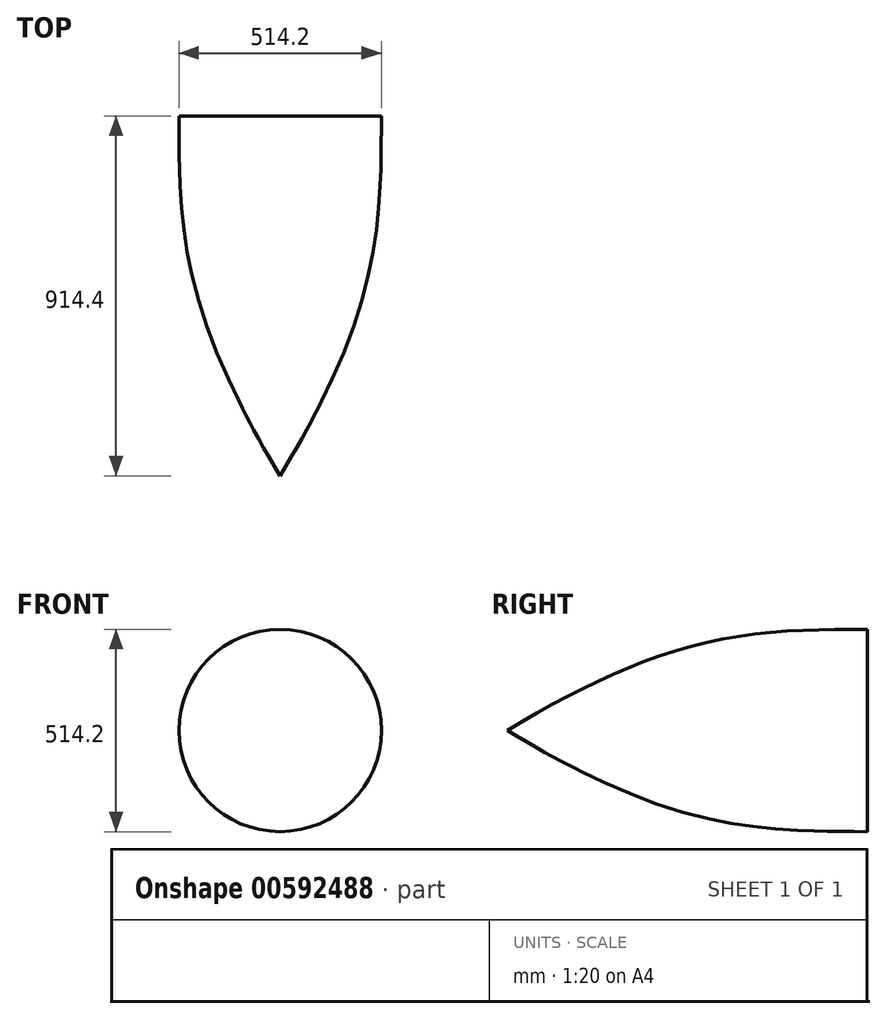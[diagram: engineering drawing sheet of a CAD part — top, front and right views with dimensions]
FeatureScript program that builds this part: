
annotation { "Feature Type Name" : "Feature", "Feature Type Description" : "" }
export const myFeature = defineFeature(function(context is Context, id is Id, definition is map)
    precondition{}
    {
        {
            var Q0;
            Q0=qCreatedBy(makeId("Right.planeOp"),FACE);
            var sketch = newSketch(context, id + "F0", { "sketchPlane" : qUnion([Q0])});
            skLineSegment(sketch, "E0", {"start": v(-457.2, 0) * mm, "end": v(457.2, 0) * mm});
            skLineSegment(sketch, "E1", {"start": v(457.2, 0) * mm, "end": v(457.2, 257.1) * mm});
            skPoint(sketch, "E2", {"position": v(-355.6, 58.93) * mm});
            skPoint(sketch, "E3", {"position": v(-254, 111.5) * mm});
            skPoint(sketch, "E4", {"position": v(-152.4, 157.78) * mm});
            skPoint(sketch, "E5", {"position": v(50.8, 223.82) * mm});
            skPoint(sketch, "E6", {"position": v(152.4, 242.32) * mm});
            skPoint(sketch, "E7", {"position": v(254, 252.63) * mm});
            skPoint(sketch, "E8", {"position": v(-50.8, 195.6) * mm});
            skPoint(sketch, "E9", {"position": v(355.6, 256.29) * mm});
            skFitSpline(sketch, "E10", {"points": [v(-457.2, 0) * mm, v(-355.6, 58.93) * mm, v(-254, 111.5) * mm, v(-152.4, 157.78) * mm, v(-50.8, 195.6) * mm, v(50.8, 223.82) * mm, v(152.4, 242.32) * mm, v(254, 252.63) * mm, v(355.6, 256.29) * mm, v(457.2, 257.1) * mm], "startDerivative": vector(871.3, 517.34) * mm, "endDerivative": vector(939.5, 3.8) * mm});
            skSolve(sketch);
        }
        {
            var Q0;
            Q0=makeQuery(id+"F0.imprint","IMPRINT",FACE,{"disambiguationData":[TD([[makeQuery(id+"F0.imprint","IMPRINT",EDGE,{"derivedFrom":sQuery(id+"F0.wireOp",EDGE,"E0")}),1.0]])]});
            var Q1;
            Q1=sQuery(id+"F0.wireOp",EDGE,"E0");
            revolve(context, id + "F1", {"entities" : qUnion([Q0]), "axis" : qUnion([Q1]), "revolveType" : RevolveType.FULL});
        }
    });
